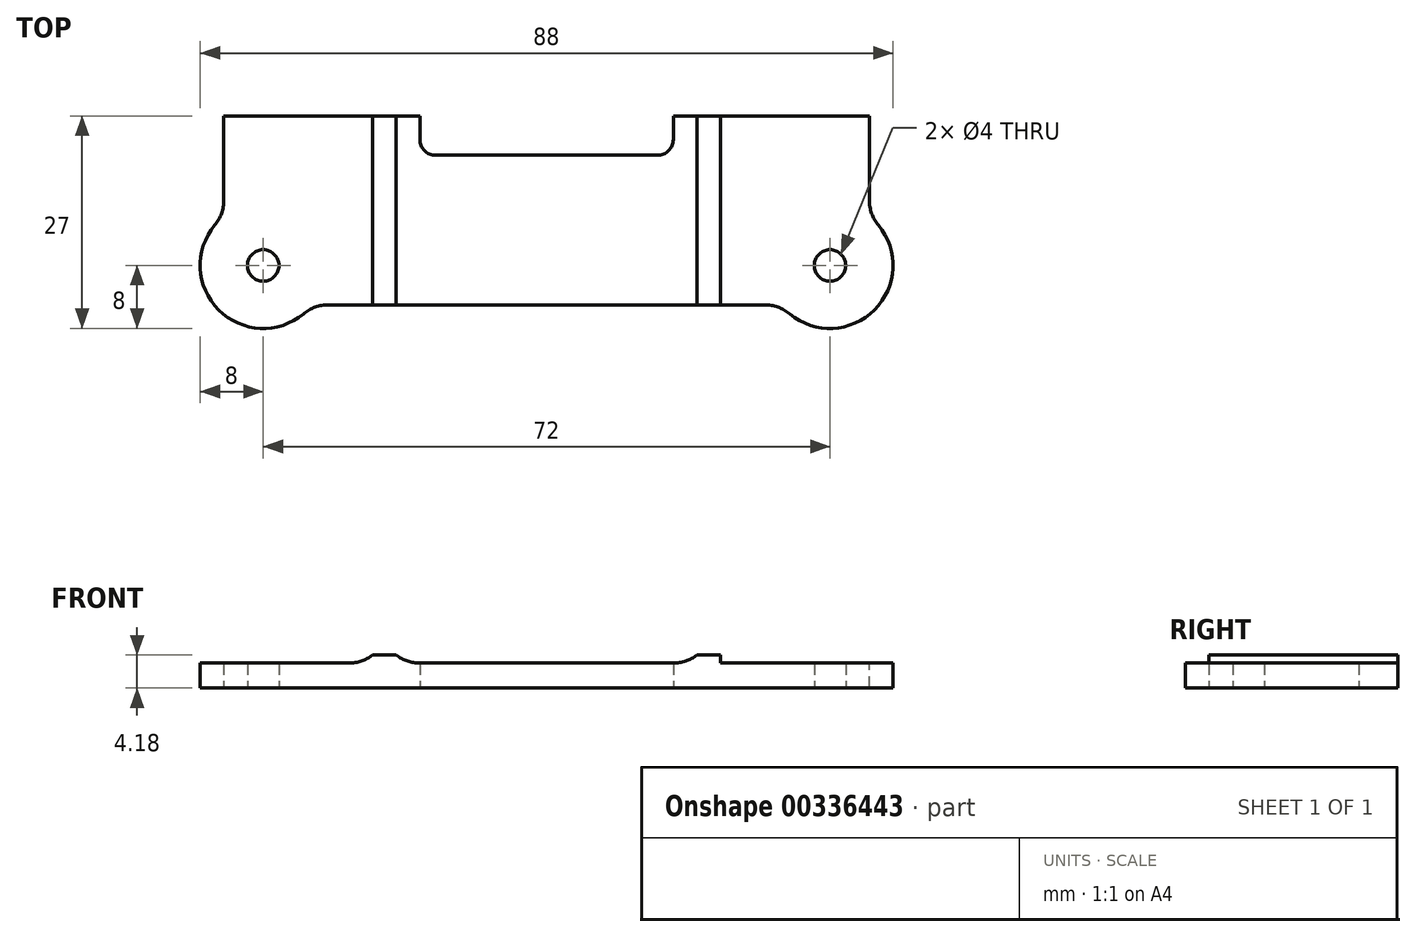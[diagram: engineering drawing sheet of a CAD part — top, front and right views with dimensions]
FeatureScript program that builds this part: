
annotation { "Feature Type Name" : "Feature", "Feature Type Description" : "" }
export const myFeature = defineFeature(function(context is Context, id is Id, definition is map)
    precondition{}
    {
        {
            var Q0;
            Q0=qCreatedBy(makeId("Top.planeOp"),FACE);
            var sketch = newSketch(context, id + "F0", { "sketchPlane" : qUnion([Q0])});
            skLineSegment(sketch, "E0", {"start": v(0, 0) * mm, "end": v(0, 24) * mm});
            skLineSegment(sketch, "E1", {"start": v(0, 24) * mm, "end": v(24.9, 24) * mm});
            skLineSegment(sketch, "E2", {"start": v(24.9, 24) * mm, "end": v(24.9, 19) * mm});
            skLineSegment(sketch, "E3", {"start": v(24.9, 19) * mm, "end": v(41, 19) * mm});
            skLineSegment(sketch, "E4", {"start": v(41, 19) * mm, "end": v(41, 0) * mm, "construction": true});
            skLineSegment(sketch, "E5", {"start": v(41, 0) * mm, "end": v(0, 0) * mm});
            skCircle(sketch, "E6", {"center": v(5, 5) * mm, "radius": 2 * mm});
            skLineSegment(sketch, "E7.MirrorCS", {"start": v(82, 0) * mm, "end": v(82, 24) * mm});
            skLineSegment(sketch, "E8.MirrorCS", {"start": v(82, 24) * mm, "end": v(57.1, 24) * mm});
            skCircle(sketch, "E9.MirrorC", {"center": v(77, 5) * mm, "radius": 2 * mm});
            skLineSegment(sketch, "E10.MirrorCS", {"start": v(57.1, 24) * mm, "end": v(57.1, 19) * mm});
            skLineSegment(sketch, "E11.MirrorCS", {"start": v(57.1, 19) * mm, "end": v(41, 19) * mm});
            skLineSegment(sketch, "E12.MirrorCS", {"start": v(41, 0) * mm, "end": v(82, 0) * mm});
            skArc(sketch, "E13", {"start": v(0, 11.24) * mm, "mid": v(-0.66, -0.66) * mm, "end": v(11.24, 0) * mm});
            skLineSegment(sketch, "E14", {"start": v(0, 11.24) * mm, "end": v(0, 0) * mm, "construction": true});
            skArc(sketch, "E15.MirrorCS", {"start": v(82, 11.24) * mm, "mid": v(82.66, -0.66) * mm, "end": v(70.76, 0) * mm});
            skSolve(sketch);
        }
        {
            var Q0;
            Q0=qSketchRegion(id+"F0",true);
            extrude(context, id + "F1", {"entities" : qUnion([Q0]), "depth" : 3.17 * mm});
        }
        {
            var Q0;
            Q0=makeQuery(id+"F1.opExtrude","SWEPT_EDGE",EDGE,{"disambiguationData":[OSD([sQuery(id+"F0.wireOp",EDGE,"E5"),sQuery(id+"F0.wireOp",EDGE,"E13")])]});
            var Q1;
            Q1=makeQuery(id+"F1.opExtrude","SWEPT_EDGE",EDGE,{"disambiguationData":[OSD([sQuery(id+"F0.wireOp",EDGE,"E12.MirrorCS"),sQuery(id+"F0.wireOp",EDGE,"E15.MirrorCS")])]});
            var Q2;
            Q2=makeQuery(id+"F1.opExtrude","SWEPT_EDGE",EDGE,{"disambiguationData":[OSD([sQuery(id+"F0.wireOp",EDGE,"E7.MirrorCS"),sQuery(id+"F0.wireOp",EDGE,"E15.MirrorCS")])]});
            var Q3;
            Q3=makeQuery(id+"F1.opExtrude","SWEPT_EDGE",EDGE,{"disambiguationData":[OSD([sQuery(id+"F0.wireOp",EDGE,"E0"),sQuery(id+"F0.wireOp",EDGE,"E13")])]});
            fillet(context, id + "F2", {"entities" : qUnion([Q0, Q1, Q2, Q3]), "radius" : 5 * mm, "tangentPropagation" : true, "allowEdgeOverflow" : false});
        }
        {
            var Q0;
            Q0=makeQuery(id+"F1.opExtrude","SWEPT_EDGE",EDGE,{"disambiguationData":[OSD([sQuery(id+"F0.wireOp",EDGE,"E2"),sQuery(id+"F0.wireOp",EDGE,"E3")])]});
            var Q1;
            Q1=makeQuery(id+"F1.opExtrude","SWEPT_EDGE",EDGE,{"disambiguationData":[OSD([sQuery(id+"F0.wireOp",EDGE,"E10.MirrorCS"),sQuery(id+"F0.wireOp",EDGE,"E11.MirrorCS")])]});
            fillet(context, id + "F3", {"entities" : qUnion([Q0, Q1]), "radius" : 2 * mm, "tangentPropagation" : true, "allowEdgeOverflow" : false});
        }
        {
            var Q0;
            Q0=makeQuery(id+"F1.opExtrude","CAP_FACE",FACE,{"disambiguationData":[OSD([sQuery(id+"F0.wireOp",EDGE,"E0"),sQuery(id+"F0.wireOp",EDGE,"E1"),sQuery(id+"F0.wireOp",EDGE,"E2"),sQuery(id+"F0.wireOp",EDGE,"E3"),sQuery(id+"F0.wireOp",EDGE,"E5"),sQuery(id+"F0.wireOp",EDGE,"E6"),sQuery(id+"F0.wireOp",EDGE,"E7.MirrorCS"),sQuery(id+"F0.wireOp",EDGE,"E8.MirrorCS"),sQuery(id+"F0.wireOp",EDGE,"E9.MirrorC"),sQuery(id+"F0.wireOp",EDGE,"E10.MirrorCS"),sQuery(id+"F0.wireOp",EDGE,"E11.MirrorCS"),sQuery(id+"F0.wireOp",EDGE,"E12.MirrorCS"),sQuery(id+"F0.wireOp",EDGE,"E13"),sQuery(id+"F0.wireOp",EDGE,"E15.MirrorCS")])],"isStart":false});
            var sketch = newSketch(context, id + "F4", { "sketchPlane" : qUnion([Q0])});
            skLineSegment(sketch, "E16", {"start": v(41, 19) * mm, "end": v(41, 0) * mm, "construction": true});
            skLineSegment(sketch, "E17", {"start": v(18.9, 0) * mm, "end": v(18.9, 24) * mm});
            skLineSegment(sketch, "E18", {"start": v(18.9, 24) * mm, "end": v(21.9, 24) * mm});
            skLineSegment(sketch, "E19", {"start": v(21.9, 24) * mm, "end": v(21.9, 0) * mm});
            skLineSegment(sketch, "E20", {"start": v(21.9, 0) * mm, "end": v(18.9, 0) * mm});
            skLineSegment(sketch, "E21.MirrorCS", {"start": v(63.1, 0) * mm, "end": v(63.1, 24) * mm});
            skLineSegment(sketch, "E22.MirrorCS", {"start": v(63.1, 24) * mm, "end": v(60.1, 24) * mm});
            skLineSegment(sketch, "E23.MirrorCS", {"start": v(60.1, 24) * mm, "end": v(60.1, 0) * mm});
            skLineSegment(sketch, "E24.MirrorCS", {"start": v(60.1, 0) * mm, "end": v(63.1, 0) * mm});
            skSolve(sketch);
        }
        {
            var Q0;
            Q0=qSketchRegion(id+"F4",true);
            extrude(context, id + "F5", {"entities" : qUnion([Q0]), "operationType" : NewBodyOperationType.ADD, "depth" : 1 * mm});
        }
        {
            var Q0;
            Q0=makeQuery(id+"F5.opExtrude","CAP_EDGE",EDGE,{"disambiguationData":[OSD([sQuery(id+"F4.wireOp",EDGE,"E17")])],"isStart":true});
            var Q1;
            Q1=makeQuery(id+"F5.opExtrude","CAP_EDGE",EDGE,{"disambiguationData":[OSD([sQuery(id+"F4.wireOp",EDGE,"E19")])],"isStart":true});
            var Q2;
            Q2=makeQuery(id+"F5.opExtrude","CAP_EDGE",EDGE,{"disambiguationData":[OSD([sQuery(id+"F4.wireOp",EDGE,"E23.MirrorCS")])],"isStart":true});
            var Q3;
            Q3=makeQuery(id+"F5.opExtrude","CAP_EDGE",EDGE,{"disambiguationData":[OSD([sQuery(id+"F4.wireOp",EDGE,"E21.MirrorCS")])],"isStart":true});
            fillet(context, id + "F6", {"entities" : qUnion([Q0, Q1, Q2, Q3]), "radius" : 5 * mm, "tangentPropagation" : true, "allowEdgeOverflow" : false});
        }
    });
